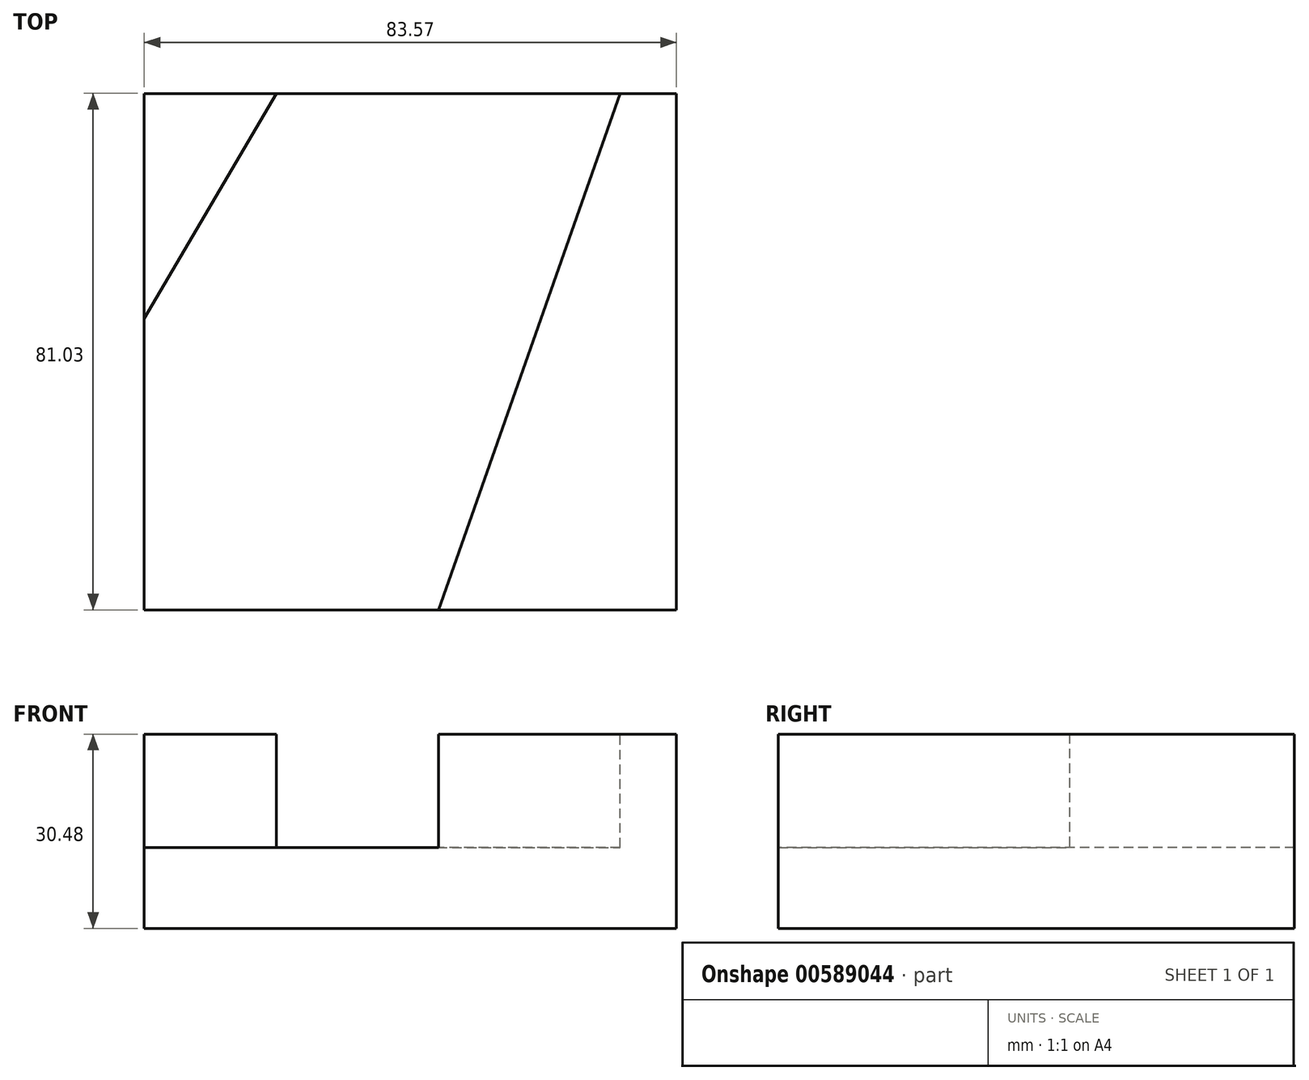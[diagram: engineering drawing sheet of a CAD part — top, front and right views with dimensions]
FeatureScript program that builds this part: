
annotation { "Feature Type Name" : "Feature", "Feature Type Description" : "" }
export const myFeature = defineFeature(function(context is Context, id is Id, definition is map)
    precondition{}
    {
        {
            var Q0;
            Q0=qCreatedBy(makeId("Front.planeOp"),FACE);
            var sketch = newSketch(context, id + "F0", { "sketchPlane" : qUnion([Q0])});
            skLineSegment(sketch, "E0", {"start": v(-57.5, 0) * mm, "end": v(-57.5, 30.48) * mm});
            skLineSegment(sketch, "E1", {"start": v(-57.5, 30.48) * mm, "end": v(-6.7, 30.48) * mm});
            skLineSegment(sketch, "E2", {"start": v(-6.7, 30.48) * mm, "end": v(-6.7, 0) * mm});
            skLineSegment(sketch, "E3", {"start": v(-6.7, 0) * mm, "end": v(-57.5, 0) * mm});
            skSolve(sketch);
        }
        {
            var Q0;
            Q0=makeQuery(id+"F0.imprint","IMPRINT",FACE,{"disambiguationData":[TD([[makeQuery(id+"F0.imprint","IMPRINT",EDGE,{"derivedFrom":sQuery(id+"F0.wireOp",EDGE,"E0")}),-1.0]])]});
            extrude(context, id + "F1", {"entities" : qUnion([Q0]), "depth" : 25.4 * mm, "offsetDistance" : 25.4 * mm});
        }
        {
            var Q0;
            Q0=makeQuery(id+"F1.opExtrude","CAP_FACE",FACE,{"disambiguationData":[OSD([sQuery(id+"F0.wireOp",EDGE,"E0"),sQuery(id+"F0.wireOp",EDGE,"E1"),sQuery(id+"F0.wireOp",EDGE,"E2"),sQuery(id+"F0.wireOp",EDGE,"E3")])],"isStart":true});
            extrude(context, id + "F2", {"entities" : qUnion([Q0]), "operationType" : NewBodyOperationType.ADD, "depth" : 55.63 * mm, "offsetDistance" : 25.4 * mm});
        }
        {
            var Q0;
            {var subQ0=sQuery(id+"F0.wireOp",EDGE,"E2");Q0=makeQuery(id+"F2.boolean.opBoolean","MERGE",FACE,{"derivedFrom":[makeQuery(id+"F1.opExtrude","SWEPT_FACE",FACE,{"disambiguationData":[OSD([subQ0])]}),makeQuery(id+"F2.opExtrude","SWEPT_FACE",FACE,{"disambiguationData":[OSD([subQ0])]})]});}
            extrude(context, id + "F3", {"entities" : qUnion([Q0]), "operationType" : NewBodyOperationType.ADD, "depth" : 32.77 * mm, "offsetDistance" : 25.4 * mm});
        }
        {
            var Q0;
            {var subQ0=sQuery(id+"F0.wireOp",EDGE,"E1");Q0=makeQuery(id+"F3.boolean.opBoolean","MERGE",FACE,{"derivedFrom":[makeQuery(id+"F2.boolean.opBoolean","MERGE",FACE,{"derivedFrom":[makeQuery(id+"F1.opExtrude","SWEPT_FACE",FACE,{"disambiguationData":[OSD([subQ0])]}),makeQuery(id+"F2.opExtrude","SWEPT_FACE",FACE,{"disambiguationData":[OSD([subQ0])]})]}),makeQuery(id+"F3.opExtrude","SWEPT_FACE",FACE,{"disambiguationData":[OSD([subQ0,sQuery(id+"F0.wireOp",EDGE,"E2")])]})]});}
            var sketch = newSketch(context, id + "F4", { "sketchPlane" : qUnion([Q0])});
            skLineSegment(sketch, "E4", {"start": v(17.21, 55.63) * mm, "end": v(-11.32, -25.4) * mm});
            skSolve(sketch);
        }
        {
            var Q0;
            {var subQ0=sQuery(id+"F4.wireOp",EDGE,"E4");Q0=makeQuery(id+"F4.imprint","IMPRINT",FACE,{"disambiguationData":[TD([[makeQuery(id+"F4.imprint","IMPRINT",EDGE,{"derivedFrom":subQ0}),-1.0]])]});}
            var sketch = newSketch(context, id + "F5", { "sketchPlane" : qUnion([Q0])});
            skLineSegment(sketch, "E5", {"start": v(-43.26, 55.67) * mm, "end": v(-56.9, 29.93) * mm});
            skSolve(sketch);
        }
        {
            var Q0;
            {var subQ0=sQuery(id+"F4.wireOp",EDGE,"E4");Q0=makeQuery(id+"F4.imprint","IMPRINT",FACE,{"disambiguationData":[TD([[makeQuery(id+"F4.imprint","IMPRINT",EDGE,{"derivedFrom":subQ0}),-1.0]])]});}
            extrude(context, id + "F6", {"entities" : qUnion([Q0]), "operationType" : NewBodyOperationType.REMOVE, "oppositeDirection" : true, "depth" : 25.4 * mm, "offsetDistance" : 25.4 * mm});
        }
        {
            var Q0;
            {var subQ0=sQuery(id+"F4.wireOp",EDGE,"E4");Q0=makeQuery(id+"F5.imprint","IMPRINT",FACE,{"disambiguationData":[TD([[makeQuery(id+"F5.imprint","IMPRINT",EDGE,{"derivedFrom":makeQuery(id+"F4.imprint","IMPRINT",EDGE,{"derivedFrom":subQ0})}),-1.0]])]});}
            extrude(context, id + "F7", {"entities" : qUnion([Q0]), "operationType" : NewBodyOperationType.REMOVE, "oppositeDirection" : true, "depth" : 25.4 * mm, "offsetDistance" : 25.4 * mm});
        }
        {
            var Q0;
            Q0=makeQuery(id+"F6.boolean.opBoolean","COPY",FACE,{"derivedFrom":makeQuery(id+"F6.opExtrude","CAP_FACE",FACE,{"disambiguationData":[OSD([sQuery(id+"F0.wireOp",EDGE,"E0"),sQuery(id+"F0.wireOp",EDGE,"E1"),sQuery(id+"F0.wireOp",EDGE,"E2"),sQuery(id+"F4.wireOp",EDGE,"E4")])],"isStart":false})});
            var sketch = newSketch(context, id + "F8", { "sketchPlane" : qUnion([Q0])});
            skLineSegment(sketch, "E6", {"start": v(-36.75, 55.63) * mm, "end": v(-57.5, 20.31) * mm});
            skSolve(sketch);
        }
        {
            var Q0;
            {var subQ0=sQuery(id+"F8.wireOp",EDGE,"E6");Q0=makeQuery(id+"F8.imprint","IMPRINT",FACE,{"disambiguationData":[TD([[makeQuery(id+"F8.imprint","IMPRINT",EDGE,{"derivedFrom":subQ0}),-1.0]])]});}
            extrude(context, id + "F9", {"entities" : qUnion([Q0]), "operationType" : NewBodyOperationType.ADD, "depth" : 25.4 * mm, "offsetDistance" : 25.4 * mm});
        }
        {
            var Q0;
            Q0=makeQuery(id+"F6.boolean.opBoolean","COPY",FACE,{"derivedFrom":makeQuery(id+"F6.opExtrude","CAP_FACE",FACE,{"disambiguationData":[OSD([sQuery(id+"F0.wireOp",EDGE,"E0"),sQuery(id+"F0.wireOp",EDGE,"E1"),sQuery(id+"F0.wireOp",EDGE,"E2"),sQuery(id+"F4.wireOp",EDGE,"E4")])],"isStart":false})});
            extrude(context, id + "F10", {"entities" : qUnion([Q0]), "operationType" : NewBodyOperationType.ADD, "depth" : 7.62 * mm, "offsetDistance" : 25.4 * mm});
        }
    });
